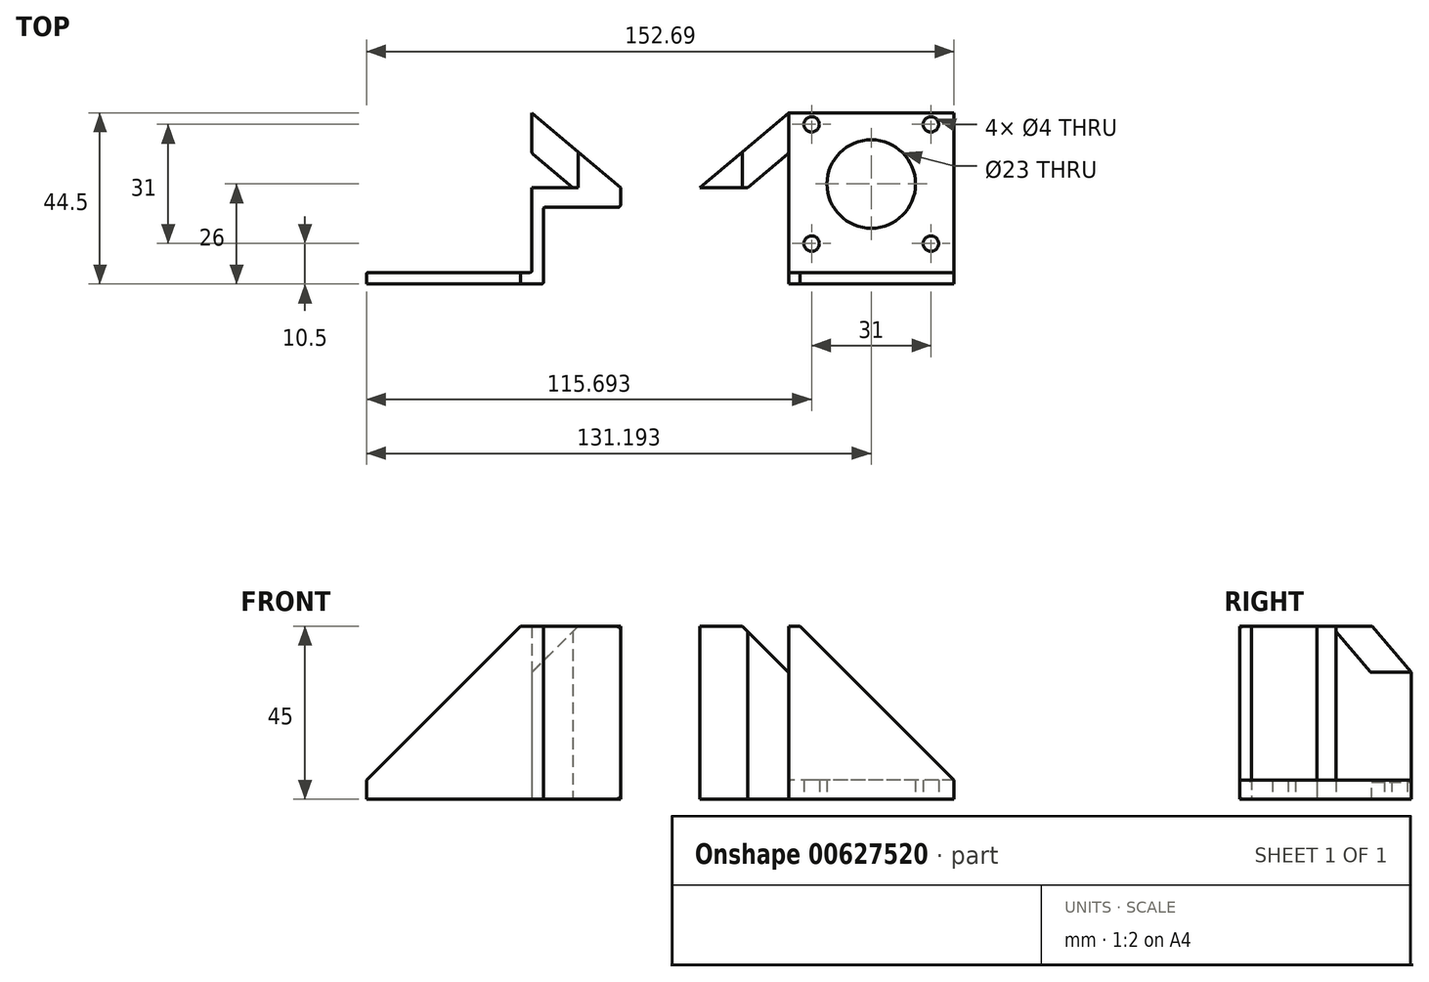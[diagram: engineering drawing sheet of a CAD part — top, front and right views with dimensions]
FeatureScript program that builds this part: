
annotation { "Feature Type Name" : "Feature", "Feature Type Description" : "" }
export const myFeature = defineFeature(function(context is Context, id is Id, definition is map)
    precondition{}
    {
        {
            var Q0;
            Q0=qCreatedBy(makeId("Top.planeOp"),FACE);
            var sketch = newSketch(context, id + "F0", { "sketchPlane" : qUnion([Q0])});
            skLineSegment(sketch, "E0.bottom", {"start": v(10, -10) * mm, "end": v(-10, -10) * mm, "construction": true});
            skLineSegment(sketch, "E0.top", {"start": v(10, 10) * mm, "end": v(-10, 10) * mm, "construction": true});
            skLineSegment(sketch, "E0.left", {"start": v(10, -10) * mm, "end": v(10, 10) * mm, "construction": true});
            skLineSegment(sketch, "E0.right", {"start": v(-10, -10) * mm, "end": v(-10, 10) * mm, "construction": true});
            skPoint(sketch, "E0.middle", {"position": v(0, 0) * mm});
            skLineSegment(sketch, "E1.bottom", {"start": v(10, 10) * mm, "end": v(-10, 10) * mm});
            skLineSegment(sketch, "E1.top", {"start": v(10, 15) * mm, "end": v(-10, 15) * mm});
            skLineSegment(sketch, "E1.left", {"start": v(10, 10) * mm, "end": v(10, 15) * mm});
            skLineSegment(sketch, "E2.bottom", {"start": v(-10, -10) * mm, "end": v(-13, -10) * mm});
            skLineSegment(sketch, "E2.top", {"start": v(-10, 15) * mm, "end": v(-13, 15) * mm});
            skLineSegment(sketch, "E2.left", {"start": v(-10, -10) * mm, "end": v(-10, 10) * mm});
            skLineSegment(sketch, "E2.right", {"start": v(-13, -10) * mm, "end": v(-13, 15) * mm});
            skLineSegment(sketch, "E3.bottom", {"start": v(-13, -10) * mm, "end": v(-56, -10) * mm});
            skLineSegment(sketch, "E3.left", {"start": v(-13, -10) * mm, "end": v(-13, 34.5) * mm});
            skLineSegment(sketch, "E3.right", {"start": v(-56, -10) * mm, "end": v(-56, 34.5) * mm});
            skLineSegment(sketch, "E4", {"start": v(-13, 34.5) * mm, "end": v(10, 15) * mm});
            skLineSegment(sketch, "E5.0", {"start": v(-13, 24.01) * mm, "end": v(-2.37, 15) * mm});
            skLineSegment(sketch, "E6", {"start": v(-56, -7) * mm, "end": v(-13, -7) * mm});
            skLineSegment(sketch, "E7", {"start": v(20.35, -33.42) * mm, "end": v(20.35, 87.93) * mm, "construction": true});
            skLineSegment(sketch, "E8.MirrorCS", {"start": v(53.7, -10) * mm, "end": v(96.7, -10) * mm});
            skLineSegment(sketch, "E9.MirrorCS", {"start": v(96.7, -7) * mm, "end": v(53.7, -7) * mm});
            skLineSegment(sketch, "E10.MirrorCS", {"start": v(53.7, -10) * mm, "end": v(53.7, 15) * mm});
            skLineSegment(sketch, "E11.MirrorCS", {"start": v(96.7, -10) * mm, "end": v(96.7, 34.5) * mm});
            skLineSegment(sketch, "E12.MirrorCS", {"start": v(53.7, 34.5) * mm, "end": v(96.7, 34.5) * mm});
            skLineSegment(sketch, "E13.MirrorCS", {"start": v(53.7, 34.5) * mm, "end": v(30.7, 15) * mm});
            skLineSegment(sketch, "E14.MirrorCS", {"start": v(30.7, 15) * mm, "end": v(50.7, 15) * mm});
            skLineSegment(sketch, "E15.MirrorCS", {"start": v(53.7, 24.01) * mm, "end": v(43.06, 15) * mm});
            skLineSegment(sketch, "E16.MirrorCS", {"start": v(30.7, 10) * mm, "end": v(50.7, 10) * mm, "construction": true});
            skLineSegment(sketch, "E17.MirrorCS", {"start": v(30.7, 10) * mm, "end": v(30.7, 15) * mm});
            skLineSegment(sketch, "E18.MirrorCS", {"start": v(53.7, -10) * mm, "end": v(53.7, 34.5) * mm});
            skLineSegment(sketch, "E19.MirrorCS", {"start": v(50.7, 15) * mm, "end": v(53.7, 15) * mm});
            skLineSegment(sketch, "E20.MirrorCS", {"start": v(50.7, -10) * mm, "end": v(50.7, 10) * mm});
            skLineSegment(sketch, "E21.MirrorCS", {"start": v(30.7, 10) * mm, "end": v(50.7, 10) * mm});
            skLineSegment(sketch, "E22.MirrorCS", {"start": v(50.7, -10) * mm, "end": v(53.7, -10) * mm});
            skCircle(sketch, "E23", {"center": v(-34.5, 16) * mm, "radius": 11.5 * mm});
            skPoint(sketch, "E23.centerSnap0", {"position": v(-34.5, 34.5) * mm});
            skCircle(sketch, "E24", {"center": v(-50, 31.5) * mm, "radius": 2 * mm});
            skCircle(sketch, "E25.0.1.0", {"center": v(-50, 0.5) * mm, "radius": 2 * mm});
            skCircle(sketch, "E25.1.0.0", {"center": v(-19, 31.5) * mm, "radius": 2 * mm});
            skCircle(sketch, "E25.1.1.0", {"center": v(-19, 0.5) * mm, "radius": 2 * mm});
            skLineSegment(sketch, "E25.direction1", {"start": v(-50, 31.5) * mm, "end": v(-19, 31.5) * mm, "construction": true});
            skLineSegment(sketch, "E25.direction2", {"start": v(-50, 31.5) * mm, "end": v(-50, 0.5) * mm, "construction": true});
            skCircle(sketch, "E26.MirrorC", {"center": v(90.7, 31.5) * mm, "radius": 2 * mm});
            skCircle(sketch, "E27.MirrorC", {"center": v(59.7, 31.5) * mm, "radius": 2 * mm});
            skCircle(sketch, "E28.MirrorC", {"center": v(59.7, 0.5) * mm, "radius": 2 * mm});
            skCircle(sketch, "E29.MirrorC", {"center": v(90.7, 0.5) * mm, "radius": 2 * mm});
            skCircle(sketch, "E30.MirrorC", {"center": v(75.2, 16) * mm, "radius": 11.5 * mm});
            skLineSegment(sketch, "E31.top", {"start": v(-56, 39.5) * mm, "end": v(-13, 39.5) * mm});
            skLineSegment(sketch, "E31.left", {"start": v(-56, 34.5) * mm, "end": v(-56, 39.5) * mm});
            skLineSegment(sketch, "E31.right", {"start": v(-13, 34.5) * mm, "end": v(-13, 39.5) * mm});
            skSolve(sketch);
        }
        {
            var Q0;
            {var subQ0=sQuery(id+"F0.wireOp",EDGE,"E4");Q0=makeQuery(id+"F0.imprint","IMPRINT",FACE,{"disambiguationData":[TD([[makeQuery(id+"F0.imprint","IMPRINT",EDGE,{"derivedFrom":subQ0}),-1.0]])]});}
            var Q1;
            Q1=makeQuery(id+"F0.imprint","IMPRINT",FACE,{"disambiguationData":[TD([[makeQuery(id+"F0.imprint","IMPRINT",EDGE,{"derivedFrom":sQuery(id+"F0.wireOp",EDGE,"E1.bottom")}),-1.0]])]});
            var Q2;
            {var subQ0=sQuery(id+"F0.wireOp",EDGE,"E3.bottom");Q2=makeQuery(id+"F0.imprint","IMPRINT",FACE,{"disambiguationData":[TD([[makeQuery(id+"F0.imprint","IMPRINT",EDGE,{"derivedFrom":subQ0}),-1.0]])]});}
            var Q3;
            {var subQ0=sQuery(id+"F0.wireOp",EDGE,"E13.MirrorCS");Q3=makeQuery(id+"F0.imprint","IMPRINT",FACE,{"disambiguationData":[TD([[makeQuery(id+"F0.imprint","IMPRINT",EDGE,{"derivedFrom":subQ0}),1.0]])]});}
            var Q4;
            {var subQ3=sQuery(id+"F0.wireOp",EDGE,"E17.MirrorCS");Q4=makeQuery(id+"F0.imprint","IMPRINT",FACE,{"disambiguationData":[TD([[makeQuery(id+"F0.imprint","IMPRINT",EDGE,{"derivedFrom":subQ3}),-1.0]])]});}
            var Q5;
            {var subQ0=sQuery(id+"F0.wireOp",EDGE,"E8.MirrorCS");Q5=makeQuery(id+"F0.imprint","IMPRINT",FACE,{"disambiguationData":[TD([[makeQuery(id+"F0.imprint","IMPRINT",EDGE,{"derivedFrom":subQ0}),1.0]])]});}
            extrude(context, id + "F1", {"entities" : qUnion([Q0, Q1, Q2, Q3, Q4, Q5]), "depth" : 45 * mm, "offsetDistance" : 25 * mm});
        }
        {
            var Q0;
            {var subQ0=sQuery(id+"F0.wireOp",EDGE,"E9.MirrorCS");Q0=makeQuery(id+"F0.imprint","IMPRINT",FACE,{"disambiguationData":[TD([[makeQuery(id+"F0.imprint","IMPRINT",EDGE,{"derivedFrom":subQ0}),-1.0]])]});}
            var Q1;
            {var subQ0=sQuery(id+"F0.wireOp",EDGE,"E6");Q1=makeQuery(id+"F0.imprint","IMPRINT",FACE,{"disambiguationData":[TD([[makeQuery(id+"F0.imprint","IMPRINT",EDGE,{"derivedFrom":subQ0}),1.0]])]});}
            extrude(context, id + "F2", {"entities" : qUnion([Q0, Q1]), "operationType" : NewBodyOperationType.ADD, "depth" : 5 * mm, "offsetDistance" : 25 * mm});
        }
        {
            var Q0;
            Q0=makeQuery(id+"F1.opExtrude","CAP_EDGE",EDGE,{"disambiguationData":[OSD([sQuery(id+"F0.wireOp",EDGE,"E3.right")])],"isStart":false});
            var Q1;
            Q1=makeQuery(id+"F1.opExtrude","CAP_EDGE",EDGE,{"disambiguationData":[OSD([sQuery(id+"F0.wireOp",EDGE,"E11.MirrorCS")])],"isStart":false});
            chamfer(context, id + "F3", {"entities" : qUnion([Q0, Q1]), "width" : 40 * mm, "tangentPropagation" : true});
        }
        {
            var Q0;
            {var subQ0=sQuery(id+"F0.wireOp",EDGE,"E3.left");Q0=makeQuery(id+"F1.opExtrude","CAP_EDGE",EDGE,{"disambiguationData":[OSD([subQ0]),TDD([makeQuery(id+"F0.imprint","IMPRINT",EDGE,{"disambiguationData":[TD([[makeQuery(id+"F0.imprint","INTERSECT",VERTEX,{"derivedFrom":[subQ0,sQuery(id+"F0.wireOp",EDGE,"E5.0")]}),-1.0]])],"derivedFrom":subQ0})])],"isStart":false});}
            var Q1;
            {var subQ0=sQuery(id+"F0.wireOp",EDGE,"E18.MirrorCS");Q1=makeQuery(id+"F1.opExtrude","CAP_EDGE",EDGE,{"disambiguationData":[OSD([subQ0]),TDD([makeQuery(id+"F0.imprint","IMPRINT",EDGE,{"disambiguationData":[TD([[makeQuery(id+"F0.imprint","INTERSECT",VERTEX,{"derivedFrom":[sQuery(id+"F0.wireOp",EDGE,"E15.MirrorCS"),subQ0]}),-1.0]])],"derivedFrom":subQ0})])],"isStart":false});}
            chamfer(context, id + "F4", {"entities" : qUnion([Q0, Q1]), "width" : 12 * mm, "tangentPropagation" : true});
        }
        {
            var Q0;
            Q0=makeQuery(id+"F1.opExtrude","SWEPT_EDGE",EDGE,{"disambiguationData":[OSD([sQuery(id+"F0.wireOp",EDGE,"E3.left"),sQuery(id+"F0.wireOp",EDGE,"E6")])]});
            var Q1;
            Q1=makeQuery(id+"F1.opExtrude","SWEPT_EDGE",EDGE,{"disambiguationData":[OSD([sQuery(id+"F0.wireOp",EDGE,"E9.MirrorCS"),sQuery(id+"F0.wireOp",EDGE,"E18.MirrorCS")])]});
            var Q2;
            {var subQ0=sQuery(id+"F0.wireOp",EDGE,"E18.MirrorCS");var subQ1=sQuery(id+"F0.wireOp",EDGE,"E9.MirrorCS");Q2=makeQuery(id+"F2.boolean.opBoolean","SPLIT",EDGE,{"disambiguationData":[topologyDisambiguationEdgeConnected([makeQuery(id+"F1.opExtrude","SWEPT_FACE",FACE,{"disambiguationData":[OSD([subQ0]),TDD([makeQuery(id+"F0.imprint","IMPRINT",EDGE,{"disambiguationData":[TD([[makeQuery(id+"F0.imprint","INTERSECT",VERTEX,{"derivedFrom":[subQ1,subQ0]}),-1.0]])],"derivedFrom":subQ0})])]})])],"derivedFrom":makeQuery(id+"F2.opExtrude","CAP_EDGE",EDGE,{"disambiguationData":[OSD([subQ0])],"isStart":false})});}
            var Q3;
            Q3=makeQuery(id+"F2.opExtrude","CAP_EDGE",EDGE,{"disambiguationData":[OSD([sQuery(id+"F0.wireOp",EDGE,"E9.MirrorCS")])],"isStart":false});
            var Q4;
            Q4=makeQuery(id+"F2.opExtrude","CAP_EDGE",EDGE,{"disambiguationData":[OSD([sQuery(id+"F0.wireOp",EDGE,"E6")])],"isStart":false});
            var Q5;
            {var subQ0=sQuery(id+"F0.wireOp",EDGE,"E3.left");var subQ1=sQuery(id+"F0.wireOp",EDGE,"E6");var subQ2=sQuery(id+"F0.wireOp",EDGE,"E31.right");Q5=makeQuery(id+"F2.boolean.opBoolean","SPLIT",EDGE,{"disambiguationData":[topologyDisambiguationEdgeConnected([makeQuery(id+"F1.opExtrude","SWEPT_FACE",FACE,{"disambiguationData":[OSD([subQ0]),TDD([makeQuery(id+"F0.imprint","IMPRINT",EDGE,{"disambiguationData":[TD([[makeQuery(id+"F0.imprint","INTERSECT",VERTEX,{"derivedFrom":[sQuery(id+"F0.wireOp",EDGE,"E2.top"),subQ0]}),1.0]])],"derivedFrom":subQ0})])]}),makeQuery(id+"F2.opExtrude","CAP_FACE",FACE,{"disambiguationData":[OSD([subQ0,sQuery(id+"F0.wireOp",EDGE,"E3.right"),subQ1,sQuery(id+"F0.wireOp",EDGE,"E23"),sQuery(id+"F0.wireOp",EDGE,"E24"),sQuery(id+"F0.wireOp",EDGE,"E25.0.1.0"),sQuery(id+"F0.wireOp",EDGE,"E25.1.0.0"),sQuery(id+"F0.wireOp",EDGE,"E25.1.1.0"),sQuery(id+"F0.wireOp",EDGE,"E31.top"),sQuery(id+"F0.wireOp",EDGE,"E31.left"),subQ2])],"isStart":false})])],"derivedFrom":makeQuery(id+"F2.opExtrude","CAP_EDGE",EDGE,{"disambiguationData":[OSD([subQ0,subQ2])],"isStart":false})});}
            var Q6;
            Q6=makeQuery(id+"F1.opExtrude","SWEPT_FACE",FACE,{"disambiguationData":[OSD([sQuery(id+"F0.wireOp",EDGE,"E2.left")])]});
            var Q7;
            Q7=makeQuery(id+"F1.opExtrude","SWEPT_FACE",FACE,{"disambiguationData":[OSD([sQuery(id+"F0.wireOp",EDGE,"E1.bottom")])]});
            var Q8;
            Q8=makeQuery(id+"F1.opExtrude","SWEPT_FACE",FACE,{"disambiguationData":[OSD([sQuery(id+"F0.wireOp",EDGE,"E20.MirrorCS")])]});
            var Q9;
            Q9=makeQuery(id+"F1.opExtrude","CAP_EDGE",EDGE,{"disambiguationData":[OSD([sQuery(id+"F0.wireOp",EDGE,"E8.MirrorCS"),sQuery(id+"F0.wireOp",EDGE,"E22.MirrorCS")])],"isStart":true});
            fillet(context, id + "F5", {"entities" : qUnion([Q0, Q1, Q2, Q3, Q4, Q5, Q6, Q7, Q8, Q9]), "radius" : 0.5 * mm, "tangentPropagation" : true, "allowEdgeOverflow" : false});
        }
    });
